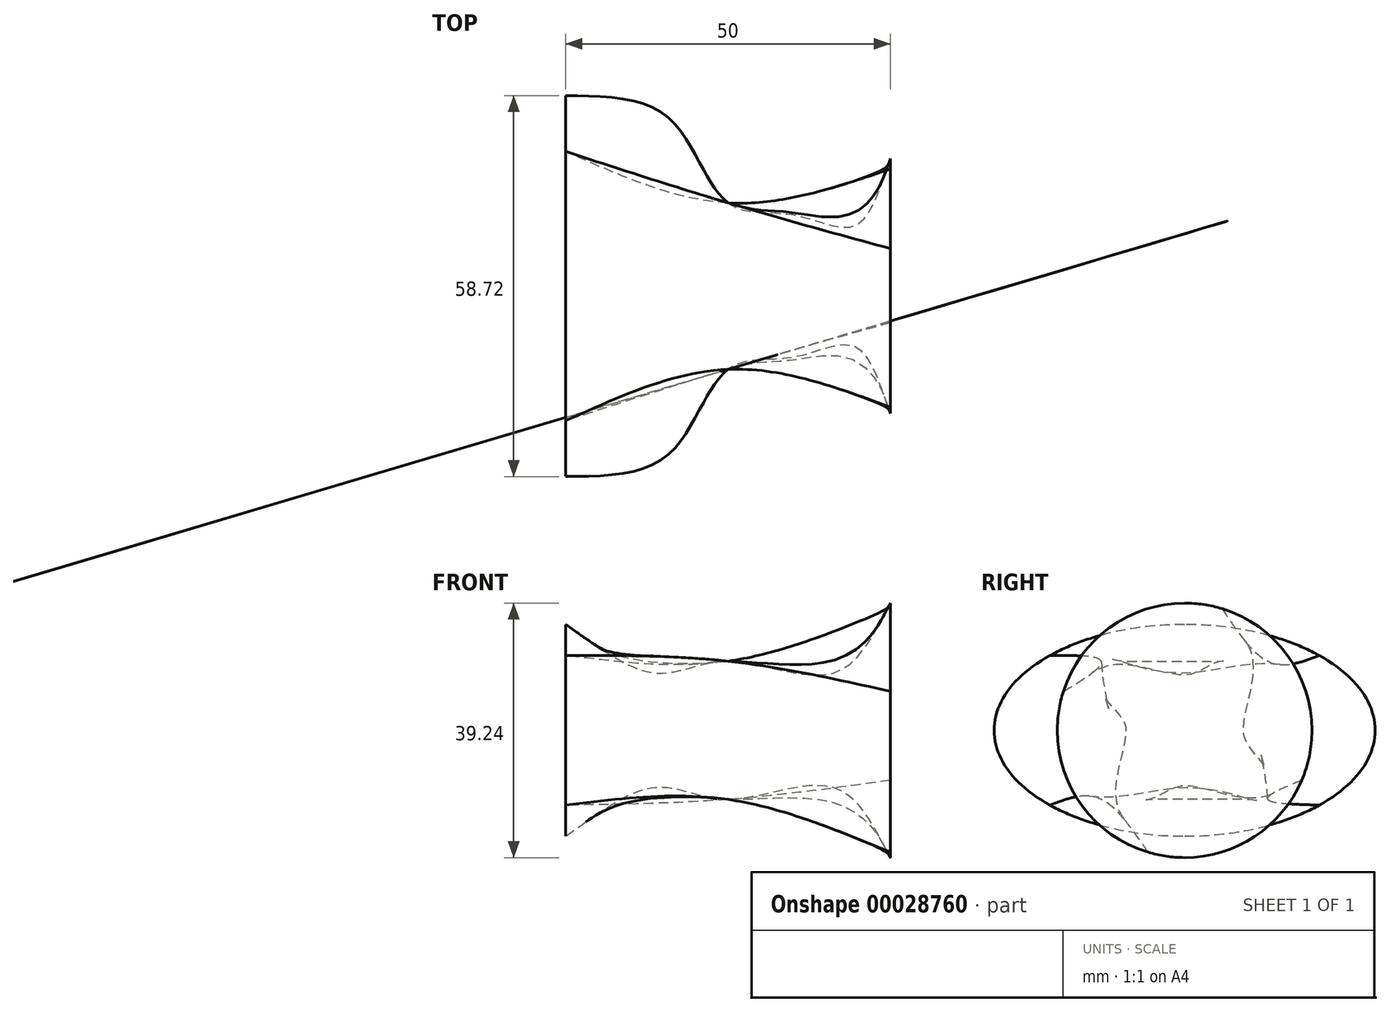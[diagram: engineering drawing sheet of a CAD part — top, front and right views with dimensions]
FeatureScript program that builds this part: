
annotation { "Feature Type Name" : "Feature", "Feature Type Description" : "" }
export const myFeature = defineFeature(function(context is Context, id is Id, definition is map)
    precondition{}
    {
        {
            var Q0;
            Q0=qCreatedBy(makeId("Right.planeOp"),FACE);
            var sketch = newSketch(context, id + "F0", { "sketchPlane" : qUnion([Q0])});
            skLineSegment(sketch, "E0", {"start": v(5.78, 18.74) * mm, "end": v(5.78, 18.74) * mm});
            skArc(sketch, "E1", {"start": v(-5.65, -18.78) * mm, "mid": v(8.3, -17.77) * mm, "end": v(18.04, -7.71) * mm});
            skArc(sketch, "E2", {"start": v(18.04, -7.71) * mm, "mid": v(17.8, 8.24) * mm, "end": v(5.78, 18.74) * mm});
            skLineSegment(sketch, "E3", {"start": v(-18.67, 6.02) * mm, "end": v(-18.67, 6.02) * mm});
            skArc(sketch, "E4", {"start": v(5.78, 18.74) * mm, "mid": v(-9.05, 17.4) * mm, "end": v(-18.67, 6.02) * mm});
            skArc(sketch, "E5", {"start": v(-18.67, 6.02) * mm, "mid": v(-17.37, -9.11) * mm, "end": v(-5.65, -18.78) * mm});
            skSolve(sketch);
        }
        {
            var Q0;
            Q0=qCreatedBy(makeId("Right.planeOp"),FACE);
            cPlane(context, id + "F1", {"entities" : qUnion([Q0]), "cplaneType" : CPlaneType.OFFSET, "offset" : 50 * mm, "oppositeDirection" : true, "width" : 150 * mm, "height" : 150 * mm});
        }
        {
            var Q0;
            Q0=qCreatedBy(id+"F1.planeOp",FACE);
            var sketch = newSketch(context, id + "F2", { "sketchPlane" : qUnion([Q0])});
            skEllipticalArc(sketch, "E6", {});
            skEllipticalArc(sketch, "E7", {});
            skEllipticalArc(sketch, "E8", {});
            skEllipticalArc(sketch, "E9", {});
            const initialGuessF2  = {"E6": [0, 0, -1, 0, 0.02935509942471981, 0.016308837055210905, 4.71238898038469, 0], "E7": [0, 0, -1, 0, 0.02935509942471981, 0.016308837055210905, 0, 1.5707963267948966], "E8": [0, 0, -1, 0, 0.02935509942471981, 0.016308837055210905, 1.5707963267948966, 3.141592653589793], "E9": [0, 0, -1, 0, 0.02935509942471981, 0.016308837055210905, 3.141592653589793, 4.71238898038469]};
            skSetInitialGuess(sketch, initialGuessF2);
            skSolve(sketch);
        }
        {
            var Q0;
            Q0=qCreatedBy(makeId("Right.planeOp"),FACE);
            cPlane(context, id + "F3", {"entities" : qUnion([Q0]), "cplaneType" : CPlaneType.OFFSET, "offset" : 25 * mm, "oppositeDirection" : true, "width" : 150 * mm, "height" : 150 * mm});
        }
        {
            var Q0;
            Q0=qCreatedBy(id+"F3.planeOp",FACE);
            var sketch = newSketch(context, id + "F4", { "sketchPlane" : qUnion([Q0])});
            skLineSegment(sketch, "E10.rect.bottom", {"start": v(12.83, -10.65) * mm, "end": v(0, -10.65) * mm});
            skLineSegment(sketch, "E10.rect.top", {"start": v(12.83, 10.65) * mm, "end": v(0, 10.65) * mm});
            skLineSegment(sketch, "E10.rect.left", {"start": v(12.83, -10.65) * mm, "end": v(12.83, 0) * mm});
            skLineSegment(sketch, "E10.rect.right", {"start": v(-12.83, -10.65) * mm, "end": v(-12.83, 0) * mm});
            skPoint(sketch, "E10.rect.middle", {"position": v(0, 0) * mm});
            skLineSegment(sketch, "E11", {"start": v(0, -10.65) * mm, "end": v(-12.83, -10.65) * mm});
            skLineSegment(sketch, "E12", {"start": v(12.83, 0) * mm, "end": v(12.83, 10.65) * mm});
            skLineSegment(sketch, "E13", {"start": v(0, 10.65) * mm, "end": v(-12.83, 10.65) * mm});
            skLineSegment(sketch, "E14", {"start": v(-12.83, 0) * mm, "end": v(-12.83, 10.65) * mm});
            skSolve(sketch);
        }
        {
            var Q0;
            Q0=qCreatedBy(makeId("Front.planeOp"),FACE);
            var sketch = newSketch(context, id + "F5", { "sketchPlane" : qUnion([Q0])});
            skFitSpline(sketch, "E15", {"points": [v(0, -19.62) * mm, v(-8.76, -8.84) * mm, v(-25, -10.65) * mm, v(-36.19, -8.84) * mm, v(-50, -16.3) * mm], "startDerivative": vector(-29, 54.76) * mm, "endDerivative": vector(-54.73, -37.52) * mm});
            skFitSpline(sketch, "E16.MirrorCS", {"points": [v(0, 19.62) * mm, v(-8.76, 8.84) * mm, v(-25, 10.65) * mm, v(-36.19, 8.84) * mm, v(-50, 16.3) * mm], "startDerivative": vector(-29, -54.76) * mm, "endDerivative": vector(-54.73, 37.52) * mm});
            skSolve(sketch);
        }
        {
            var Q0;
            Q0=qCreatedBy(makeId("Top.planeOp"),FACE);
            var sketch = newSketch(context, id + "F6", { "sketchPlane" : qUnion([Q0])});
            skFitSpline(sketch, "E17", {"points": [v(0, 19.62) * mm, v(-5.44, 9.34) * mm, v(-14.88, 10.98) * mm, v(-25, 12.83) * mm, v(-33.97, 25.76) * mm, v(-50, 29.36) * mm], "startDerivative": vector(-23.51, -65.75) * mm, "endDerivative": vector(-79.94, 0.7) * mm});
            skFitSpline(sketch, "E18.MirrorCS", {"points": [v(0, -19.62) * mm, v(-5.44, -9.34) * mm, v(-14.88, -10.98) * mm, v(-25, -12.83) * mm, v(-33.97, -25.76) * mm, v(-50, -29.36) * mm], "startDerivative": vector(-23.51, 65.75) * mm, "endDerivative": vector(-79.94, -0.7) * mm});
            skSolve(sketch);
        }
        {
            var Q0;
            Q0=makeQuery(id+"F0.imprint","IMPRINT",FACE,{"disambiguationData":[TD([[makeQuery(id+"F0.imprint","IMPRINT",EDGE,{"derivedFrom":sQuery(id+"F0.wireOp",EDGE,"E1")}),1.0]])]});
            var Q1;
            Q1=makeQuery(id+"F4.imprint","IMPRINT",FACE,{"disambiguationData":[TD([[makeQuery(id+"F4.imprint","IMPRINT",EDGE,{"derivedFrom":sQuery(id+"F4.wireOp",EDGE,"E10.rect.bottom")}),-1.0]])]});
            var Q2;
            Q2=makeQuery(id+"F2.imprint","IMPRINT",FACE,{"disambiguationData":[TD([[makeQuery(id+"F2.imprint","IMPRINT",EDGE,{"derivedFrom":sQuery(id+"F2.wireOp",EDGE,"E6")}),1.0]])]});
            var Q3;
            Q3=sQuery(id+"F6.wireOp",EDGE,"E17");
            var Q4;
            Q4=sQuery(id+"F5.wireOp",EDGE,"E15");
            var Q5;
            Q5=sQuery(id+"F5.wireOp",EDGE,"E16.MirrorCS");
            var Q6;
            Q6=sQuery(id+"F6.wireOp",EDGE,"E18.MirrorCS");
            loft(context, id + "F7", {"addGuides" : true, "sheetProfilesArray" : [{ "sheetProfileEntities" : qUnion([Q0]) }, { "sheetProfileEntities" : qUnion([Q1]) }, { "sheetProfileEntities" : qUnion([Q2]) }], "guidesArray" : [{ "guideEntities" : qUnion([Q3]), "guideDerivativeType" : LoftGuideDerivativeType.DEFAULT, "guideDerivativeMagnitude" : 1 }, { "guideEntities" : qUnion([Q4]), "guideDerivativeType" : LoftGuideDerivativeType.DEFAULT, "guideDerivativeMagnitude" : 1 }, { "guideEntities" : qUnion([Q5]), "guideDerivativeType" : LoftGuideDerivativeType.DEFAULT, "guideDerivativeMagnitude" : 1 }, { "guideEntities" : qUnion([Q6]), "guideDerivativeType" : LoftGuideDerivativeType.DEFAULT, "guideDerivativeMagnitude" : 1 }]});
        }
    });
